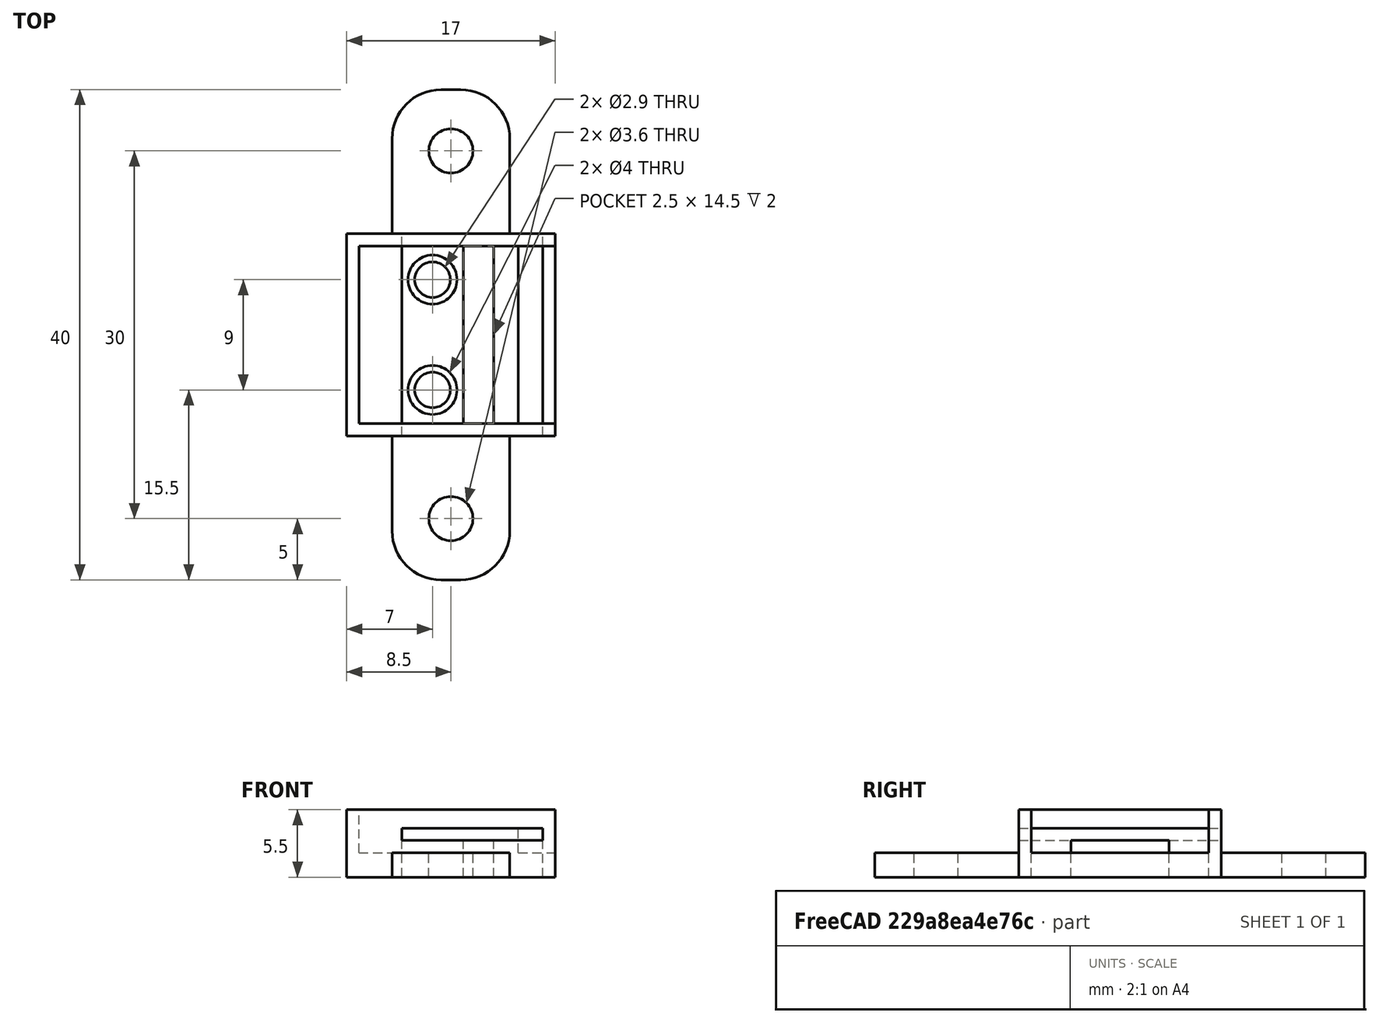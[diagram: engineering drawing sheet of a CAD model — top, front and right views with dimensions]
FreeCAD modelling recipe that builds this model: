
FCSTD DOCUMENT  (FreeCAD 0.18.4R)
Label: microusb
License: FreeArt
LicenseURL: http://artlibre.org/licence/lal
objects: Part::Box×9, Part::Cut×4, Part::Cylinder×3, Part::FeaturePython×3, Part::MultiFuse×3, App::Part×2, Spreadsheet::Sheet×1, Part::Fillet×1
note: 23 computed .brp shape members not serialized (recipe doc carries the construction recipe); baked Part::Feature solids carry a one-line shape summary decoded from their .brp

FEATURE [Spreadsheet::Sheet] Spreadsheet001  label="p"
  cells = A1=pcb_x; B1(pcb_x)=16; A2=pcb_y; B2(pcb_y)=14.5; A3=pcb_h; B3(pcb_h)=1.5; A4=pcb_under; B4(pcb_under)=2; A5=underlayer; B5(underlayer)=2; A6=side_wall; B6(side_wall)=1; A7=hole_r; B7(hole_r)=1.45; A8=hole_dist; B8(hole_dist)=9; A9=hole_off; B9(hole_off)=6; A10=hole_stand_x; B10(hole_stand_x)=5; A11=hole_stand_off; B11(hole_stand_off)=3.5; A12=pcb_underplate_x; B12(pcb_underplate_x)=2; A13=pcb_underplate_off; B13(pcb_underplate_off)=11; A14=attach_hole_dist; B14(attach_hole_dist)=10; A15=attach_hole_r; B15(attach_hole_r)=1.8; A16=attach_hole_wall; B16(attach_hole_wall)=3; A17=microusb_h; B17(microusb_h)=3; A18=microusb_y; B18(microusb_y)=8; A19=microusb_x; B19(microusb_x)=5; A20=bolt_hole_r; B20(bolt_hole_r)=2
FEATURE [Part::Box] Box  label="bottom cube"
  AttacherType = Attacher::AttachEngine3D
  Height = 5.5
  Length = 17
  Width = 16.5
  expr: Width = p.pcb_y + p.side_wall * 2
  expr: Length = p.pcb_x + p.side_wall
  expr: Height = p.underlayer + p.pcb_under + p.pcb_h
FEATURE [Part::Box] Box001  label="bottom cube extract"
  AttacherType = Attacher::AttachEngine3D
  Height = 3.5
  Length = 16
  Placement = pos=(1,1,2) rot=(0,0,1;0rad)
  Width = 14.5
  expr: Placement.Base.x = p.side_wall
  expr: Placement.Base.y = p.side_wall
  expr: Placement.Base.z = p.underlayer
  expr: Height = p.pcb_h + p.pcb_under
  expr: Width = p.pcb_y
  expr: Length = p.pcb_x
FEATURE [Part::Cut] Cut  label="bottom cut"
  Base = -> Box
  Tool = -> Box001
FEATURE [Part::Box] Box002  label="hole stand cube"
  AttacherType = Attacher::AttachEngine3D
  Height = 2
  Length = 5
  Placement = pos=(4.5,1,2) rot=(0,0,1;0rad)
  Width = 14.5
  expr: Placement.Base.x = p.side_wall + p.hole_stand_off
  expr: Placement.Base.y = p.side_wall
  expr: Placement.Base.z = p.underlayer
  expr: Height = p.pcb_under
  expr: Width = p.pcb_y
  expr: Length = p.hole_stand_x
FEATURE [Part::Box] Box003  label="underplate cube"
  AttacherType = Attacher::AttachEngine3D
  Height = 2
  Length = 2
  Placement = pos=(12,1,2) rot=(0,0,1;0rad)
  Width = 14.5
  expr: Placement.Base.x = p.side_wall + p.pcb_underplate_off
  expr: Placement.Base.y = p.side_wall
  expr: Placement.Base.z = p.underlayer
  expr: Height = p.pcb_under
  expr: Width = p.pcb_y
  expr: Length = p.pcb_underplate_x
FEATURE [Part::Cylinder] Cylinder  label="pcb hole"
  Angle = 360
  AttacherType = Attacher::AttachEngine3D
  Height = 20
  Placement = pos=(7,3.75,0) rot=(0,0,1;0rad)
  Radius = 1.45
  expr: Placement.Base.x = p.side_wall + p.hole_off
  expr: Placement.Base.y = p.side_wall + (p.pcb_y - p.hole_dist) / 2
  expr: Radius = p.hole_r
FEATURE [Part::FeaturePython] Array  label="hole array"  # Draft array (typed FeaturePython)
  Angle = 360
  ArrayType = 0
  Axis = (0,0,1)
  Base = -> Cylinder
  Center = (0,0,0)
  Fuse = false
  IntervalAxis = (0,0,0)
  IntervalX = (1,0,0)
  IntervalY = (0,9,0)
  IntervalZ = (0,0,1)
  NumberPolar = 1
  NumberX = 1
  NumberY = 2
  NumberZ = 1
  expr: IntervalY.y = p.hole_dist
FEATURE [Part::Box] Box004  label="ears cube"
  AttacherType = Attacher::AttachEngine3D
  Height = 2
  Length = 9.6
  Width = 40
  expr: Length = (p.attach_hole_r + p.attach_hole_wall) * 2
  expr: Width = floor(p.pcb_x / p.attach_hole_dist + 3) * p.attach_hole_dist
  expr: Height = p.underlayer
FEATURE [Part::Fillet] Fillet  label="ears cube fillet"
  Base = -> Box004
  Edges = 4 edges r=4: [Edge1,Edge3,Edge5,Edge7]
FEATURE [Part::Cylinder] Cylinder001  label="attach hole"
  Angle = 360
  AttacherType = Attacher::AttachEngine3D
  Height = 10
  Placement = pos=(4.8,5,0) rot=(0,0,1;0rad)
  Radius = 1.8
  expr: Placement.Base.x = p.attach_hole_r + p.attach_hole_wall
  expr: Placement.Base.y = p.attach_hole_dist / 2
  expr: Radius = p.attach_hole_r
FEATURE [Part::FeaturePython] Array002  label="attach hole array"  # Draft array (typed FeaturePython)
  Angle = 360
  ArrayType = 0
  Axis = (0,0,1)
  Base = -> Cylinder001
  Center = (0,0,0)
  Fuse = false
  IntervalAxis = (0,0,0)
  IntervalX = (1,0,0)
  IntervalY = (0,30,0)
  IntervalZ = (0,0,1)
  NumberPolar = 1
  NumberX = 1
  NumberY = 2
  NumberZ = 1
  expr: IntervalY.y = floor(p.pcb_y / p.attach_hole_dist + 2) * p.attach_hole_dist
FEATURE [Part::Cut] Cut002  label="attach plane"
  Base = -> Fillet
  Placement = pos=(3.7,-11.75,0) rot=(0,0,1;0rad)
  Tool = -> Array002
  expr: Placement.Base.y = -(floor(p.pcb_y / p.attach_hole_dist + 3) * p.attach_hole_dist - 2 * p.side_wall - p.pcb_y) / 2
  expr: Placement.Base.x = (p.side_wall + p.pcb_x - (p.attach_hole_r + p.attach_hole_wall) * 2) / 2
FEATURE [Part::MultiFuse] Fusion  label="bottom fusion"
  Shapes = -> [Cut,Box002,Box003,Cut002]
FEATURE [Part::Cut] Cut001  label="microusb upper cut"
  Base = -> Fusion
  Tool = -> Array
FEATURE [App::Part] Part001  label="microusb part"
  Group = -> [Array,Box001,Cylinder,Cut,Box,Fillet,Box003,Fusion,Box002,Array002,Cut002,Cylinder001,Box004,Cut001]
  Origin = -> Origin001
FEATURE [Part::Box] Box005  label="top cover cube"
  AttacherType = Attacher::AttachEngine3D
  Height = 1
  Length = 11.5
  Placement = pos=(4.5,0,3) rot=(0,0,1;0rad)
  Width = 16.5
  expr: Placement.Base.x = p.side_wall + p.hole_stand_off
  expr: Length = p.pcb_x - p.hole_stand_off - p.side_wall
  expr: Width = p.side_wall * 2 + p.pcb_y
  expr: Placement.Base.z = p.microusb_h
  expr: Height = p.side_wall
FEATURE [Part::Box] Box006  label="hole stand cube001"
  AttacherType = Attacher::AttachEngine3D
  Height = 3
  Length = 5
  Placement = pos=(4.5,1,0) rot=(0,0,1;0rad)
  Width = 14.5
  expr: Placement.Base.x = p.side_wall + p.hole_stand_off
  expr: Placement.Base.y = p.side_wall
  expr: Height = p.microusb_h
  expr: Width = p.pcb_y
  expr: Length = p.hole_stand_x
FEATURE [Part::Box] Box007  label="usb side protection cube"
  AttacherType = Attacher::AttachEngine3D
  Height = 3
  Length = 4
  Placement = pos=(12,1,0) rot=(0,0,1;0rad)
  Width = 14.5
  expr: Placement.Base.x = p.side_wall + p.pcb_x - p.microusb_x
  expr: Placement.Base.y = p.side_wall
  expr: Height = p.microusb_h
  expr: Width = p.pcb_y
  expr: Length = p.microusb_x - 1
FEATURE [Part::MultiFuse] Fusion001  label="protector fusion"
  Shapes = -> [Box005,Box006,Box007]
FEATURE [Part::Box] Box008  label="microusb extraction"
  AttacherType = Attacher::AttachEngine3D
  Height = 3
  Length = 5
  Placement = pos=(12,4.25,0) rot=(0,0,1;0rad)
  Width = 8
  expr: Placement.Base.y = (p.side_wall * 2 + p.pcb_y - p.microusb_y) / 2
  expr: Placement.Base.x = p.side_wall + p.pcb_x - p.microusb_x
  expr: Height = p.microusb_h
  expr: Width = p.microusb_y
  expr: Length = p.microusb_x
FEATURE [Part::Cylinder] Cylinder002  label="pcb hole001"
  Angle = 360
  AttacherType = Attacher::AttachEngine3D
  Height = 20
  Placement = pos=(7,3.75,0) rot=(0,0,1;0rad)
  Radius = 2
  expr: Placement.Base.x = p.side_wall + p.hole_off
  expr: Placement.Base.y = p.side_wall + (p.pcb_y - p.hole_dist) / 2
  expr: Radius = p.bolt_hole_r
FEATURE [Part::FeaturePython] Array003  label="hole array copy"  # Draft array (typed FeaturePython)
  Angle = 360
  ArrayType = 0
  Axis = (0,0,1)
  Base = -> Cylinder002
  Center = (0,0,0)
  Fuse = false
  IntervalAxis = (0,0,0)
  IntervalX = (1,0,0)
  IntervalY = (0,9,0)
  IntervalZ = (0,0,1)
  NumberPolar = 1
  NumberX = 1
  NumberY = 2
  NumberZ = 1
  expr: IntervalY.y = p.hole_dist
FEATURE [Part::MultiFuse] Fusion002  label="protector extraction fusion"
  Shapes = -> [Box008,Array003]
FEATURE [Part::Cut] Cut003  label="protector cut"
  Base = -> Fusion001
  Tool = -> Fusion002
FEATURE [App::Part] Part  label="top protection part"
  Group = -> [Box005,Box006,Fusion001,Cut003]
  Origin = -> Origin
  Placement = pos=(0,0,6) rot=(0,0,1;0rad)
